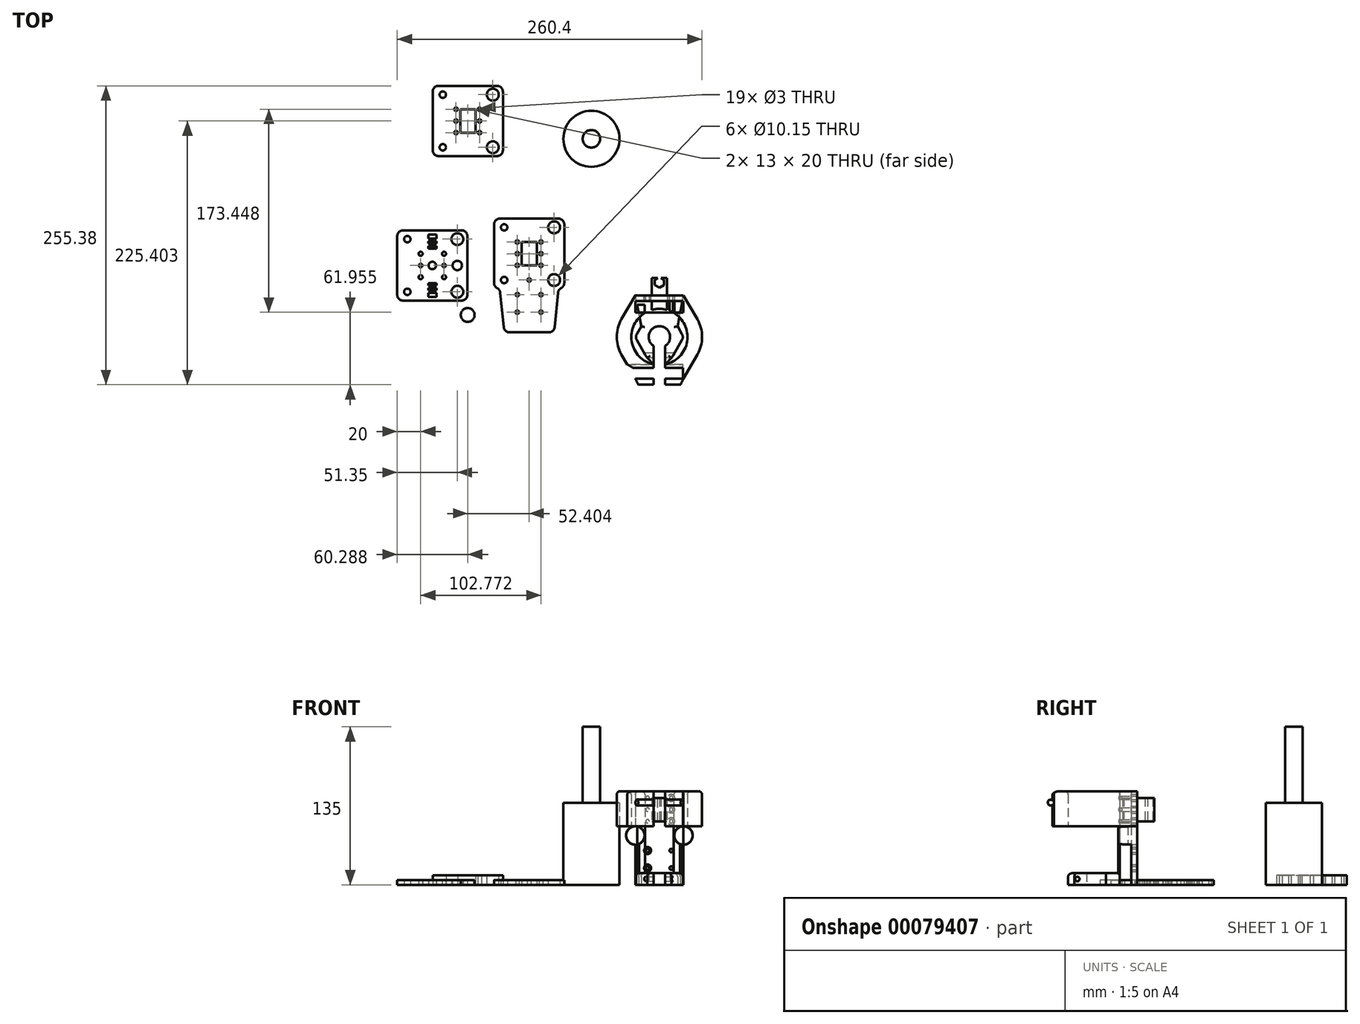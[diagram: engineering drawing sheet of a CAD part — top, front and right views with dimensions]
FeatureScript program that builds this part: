
annotation { "Feature Type Name" : "Feature", "Feature Type Description" : "" }
export const myFeature = defineFeature(function(context is Context, id is Id, definition is map)
    precondition{}
    {
        {
            var Q0;
            Q0=qCreatedBy(makeId("Top.planeOp"),FACE);
            var sketch = newSketch(context, id + "F0", { "sketchPlane" : qUnion([Q0])});
            skArc(sketch, "E0", {"start": v(24.79, -19.87) * mm, "mid": v(28.33, -18.4) * mm, "end": v(29.79, -14.87) * mm});
            skLineSegment(sketch, "E1", {"start": v(24.79, -19.87) * mm, "end": v(-25.21, -19.87) * mm});
            skArc(sketch, "E2", {"start": v(29.79, 35.13) * mm, "mid": v(28.33, 38.67) * mm, "end": v(24.79, 40.13) * mm});
            skLineSegment(sketch, "E3", {"start": v(29.79, 35.13) * mm, "end": v(29.79, -14.87) * mm});
            skArc(sketch, "E4", {"start": v(-25.21, 40.13) * mm, "mid": v(-28.75, 38.67) * mm, "end": v(-30.21, 35.13) * mm});
            skLineSegment(sketch, "E5", {"start": v(-25.21, 40.13) * mm, "end": v(24.79, 40.13) * mm});
            skArc(sketch, "E6", {"start": v(-30.21, -14.87) * mm, "mid": v(-28.75, -18.4) * mm, "end": v(-25.21, -19.87) * mm});
            skLineSegment(sketch, "E7", {"start": v(-30.21, -14.87) * mm, "end": v(-30.21, 35.13) * mm});
            skCircle(sketch, "E8", {"center": v(30, -32.16) * mm, "radius": 5.9 * mm});
            skCircle(sketch, "E9", {"center": v(-30, -32.16) * mm, "radius": 5.9 * mm});
            skLineSegment(sketch, "E10", {"start": v(-30.85, -40.13) * mm, "end": v(30.85, -40.13) * mm});
            skArc(sketch, "E11", {"start": v(30.85, -40.13) * mm, "mid": v(36.61, -37.74) * mm, "end": v(39, -31.98) * mm});
            skArc(sketch, "E12", {"start": v(39, -31.98) * mm, "mid": v(36.61, -26.22) * mm, "end": v(30.85, -23.83) * mm});
            skLineSegment(sketch, "E13", {"start": v(30.85, -23.83) * mm, "end": v(-30.85, -23.83) * mm});
            skArc(sketch, "E14", {"start": v(-30.85, -23.83) * mm, "mid": v(-36.61, -26.22) * mm, "end": v(-39, -31.98) * mm});
            skArc(sketch, "E15", {"start": v(-39, -31.98) * mm, "mid": v(-36.61, -37.74) * mm, "end": v(-30.85, -40.13) * mm});
            skCircle(sketch, "E16", {"center": v(21.14, 32.63) * mm, "radius": 5.08 * mm});
            skCircle(sketch, "E17", {"center": v(21.14, -12.37) * mm, "radius": 5.08 * mm});
            skCircle(sketch, "E18", {"center": v(-21.56, 32.63) * mm, "radius": 2.75 * mm});
            skCircle(sketch, "E19", {"center": v(-21.56, -12.37) * mm, "radius": 2.75 * mm});
            skCircle(sketch, "E20", {"center": v(-10.21, 20.13) * mm, "radius": 1.75 * mm});
            skCircle(sketch, "E21", {"center": v(-10.21, 0.13) * mm, "radius": 1.75 * mm});
            skCircle(sketch, "E22", {"center": v(9.79, 0.13) * mm, "radius": 1.75 * mm});
            skCircle(sketch, "E23", {"center": v(9.79, 20.13) * mm, "radius": 1.75 * mm});
            skLineSegment(sketch, "E24", {"start": v(-3.63, -6.88) * mm, "end": v(3.37, -6.88) * mm});
            skLineSegment(sketch, "E25", {"start": v(3.37, -6.88) * mm, "end": v(3.37, -4.88) * mm});
            skLineSegment(sketch, "E26", {"start": v(3.37, -4.88) * mm, "end": v(-3.63, -4.88) * mm});
            skLineSegment(sketch, "E27", {"start": v(-3.63, -4.88) * mm, "end": v(-3.63, -6.88) * mm});
            skLineSegment(sketch, "E28", {"start": v(-3.66, -11.08) * mm, "end": v(3.34, -11.08) * mm});
            skLineSegment(sketch, "E29", {"start": v(3.34, -11.08) * mm, "end": v(3.34, -9.08) * mm});
            skLineSegment(sketch, "E30", {"start": v(3.34, -9.08) * mm, "end": v(-3.66, -9.08) * mm});
            skLineSegment(sketch, "E31", {"start": v(-3.66, -9.08) * mm, "end": v(-3.66, -11.08) * mm});
            skLineSegment(sketch, "E32", {"start": v(3.35, -16.82) * mm, "end": v(3.35, -13.38) * mm});
            skLineSegment(sketch, "E33", {"start": v(3.35, -13.38) * mm, "end": v(-3.63, -13.38) * mm});
            skLineSegment(sketch, "E34", {"start": v(-3.63, 33.12) * mm, "end": v(3.37, 33.12) * mm});
            skLineSegment(sketch, "E35", {"start": v(3.37, 33.12) * mm, "end": v(3.37, 36.53) * mm});
            skLineSegment(sketch, "E36", {"start": v(3.37, 36.53) * mm, "end": v(-3.63, 36.52) * mm});
            skLineSegment(sketch, "E37", {"start": v(-3.63, 36.52) * mm, "end": v(-3.63, 33.12) * mm});
            skLineSegment(sketch, "E38", {"start": v(-3.66, 28.92) * mm, "end": v(3.34, 28.92) * mm});
            skLineSegment(sketch, "E39", {"start": v(3.34, 28.92) * mm, "end": v(3.34, 30.92) * mm});
            skLineSegment(sketch, "E40", {"start": v(3.34, 30.92) * mm, "end": v(-3.66, 30.92) * mm});
            skLineSegment(sketch, "E41", {"start": v(-3.66, 30.92) * mm, "end": v(-3.66, 28.92) * mm});
            skLineSegment(sketch, "E42", {"start": v(-3.63, 24.62) * mm, "end": v(3.37, 24.62) * mm});
            skLineSegment(sketch, "E43", {"start": v(3.37, 24.62) * mm, "end": v(3.37, 26.62) * mm});
            skLineSegment(sketch, "E44", {"start": v(3.37, 26.62) * mm, "end": v(-3.63, 26.62) * mm});
            skLineSegment(sketch, "E45", {"start": v(-3.63, 26.62) * mm, "end": v(-3.63, 24.62) * mm});
            skCircle(sketch, "E46", {"center": v(-10.21, 10.13) * mm, "radius": 1.5 * mm});
            skCircle(sketch, "E47", {"center": v(9.79, 10.13) * mm, "radius": 1.5 * mm});
            skCircle(sketch, "E48", {"center": v(-10.18, -31.98) * mm, "radius": 1.5 * mm});
            skCircle(sketch, "E49", {"center": v(9.82, -31.98) * mm, "radius": 1.5 * mm});
            skCircle(sketch, "E50", {"center": v(-0.21, 10.13) * mm, "radius": 3.2 * mm});
            skPoint(sketch, "E51", {"position": v(-3.63, 36.52) * mm});
            skLineSegment(sketch, "E52", {"start": v(-3.63, -16.82) * mm, "end": v(3.35, -16.82) * mm});
            skLineSegment(sketch, "E53", {"start": v(-3.63, -16.82) * mm, "end": v(-3.63, -13.38) * mm});
            skCircle(sketch, "E54", {"center": v(21.14, 10.13) * mm, "radius": 4 * mm});
            skLineSegment(sketch, "E55", {"start": v(112.48, 45.2) * mm, "end": v(112.48, -4.8) * mm});
            skLineSegment(sketch, "E56", {"start": v(57.48, 50.2) * mm, "end": v(107.48, 50.2) * mm});
            skLineSegment(sketch, "E57", {"start": v(52.48, -4.8) * mm, "end": v(52.48, 45.2) * mm});
            skCircle(sketch, "E58", {"center": v(103.83, 42.7) * mm, "radius": 5.08 * mm});
            skCircle(sketch, "E59", {"center": v(103.83, -2.3) * mm, "radius": 5.08 * mm});
            skCircle(sketch, "E60", {"center": v(61.13, -2.3) * mm, "radius": 2.75 * mm});
            skCircle(sketch, "E61", {"center": v(61.13, 42.7) * mm, "radius": 2.75 * mm});
            skArc(sketch, "E62", {"start": v(109.8, -9.23) * mm, "mid": v(111.76, -7.4) * mm, "end": v(112.48, -4.8) * mm});
            skArc(sketch, "E63", {"start": v(112.48, 45.2) * mm, "mid": v(111.02, 48.73) * mm, "end": v(107.48, 50.2) * mm});
            skArc(sketch, "E64", {"start": v(57.48, 50.2) * mm, "mid": v(53.95, 48.73) * mm, "end": v(52.48, 45.2) * mm});
            skArc(sketch, "E65", {"start": v(52.48, -4.8) * mm, "mid": v(53.95, -8.34) * mm, "end": v(57.48, -9.8) * mm});
            skLineSegment(sketch, "E66", {"start": v(82.48, -47) * mm, "end": v(82.48, -9.8) * mm, "construction": true});
            skLineSegment(sketch, "E67", {"start": v(82.48, -47) * mm, "end": v(99.3, -47) * mm});
            skLineSegment(sketch, "E68", {"start": v(107.15, -13.17) * mm, "end": v(104.27, -42.49) * mm});
            skPoint(sketch, "E69.visualSharp", {"position": v(107.48, -9.8) * mm});
            skArc(sketch, "E69.filletArc", {"start": v(109.8, -9.23) * mm, "mid": v(107.98, -10.87) * mm, "end": v(107.15, -13.17) * mm});
            skPoint(sketch, "E70.visualSharp", {"position": v(103.83, -47) * mm});
            skArc(sketch, "E70.filletArc", {"start": v(99.3, -47) * mm, "mid": v(102.66, -45.7) * mm, "end": v(104.27, -42.49) * mm});
            skLineSegment(sketch, "E71.MirrorCS", {"start": v(82.48, -47) * mm, "end": v(65.66, -47) * mm});
            skArc(sketch, "E72.MirrorCS", {"start": v(65.66, -47) * mm, "mid": v(62.3, -45.7) * mm, "end": v(60.69, -42.49) * mm});
            skLineSegment(sketch, "E73.MirrorCS", {"start": v(57.81, -13.17) * mm, "end": v(60.69, -42.49) * mm});
            skArc(sketch, "E74.MirrorCS", {"start": v(55.16, -9.23) * mm, "mid": v(56.98, -10.87) * mm, "end": v(57.81, -13.17) * mm});
            skLineSegment(sketch, "E75", {"start": v(82.48, 30.21) * mm, "end": v(87.48, 30.21) * mm});
            skLineSegment(sketch, "E76.bottom", {"start": v(87.48, 30.21) * mm, "end": v(77.48, 30.21) * mm});
            skLineSegment(sketch, "E77", {"start": v(92.56, 30.21) * mm, "end": v(92.56, 10.21) * mm, "construction": true});
            skLineSegment(sketch, "E78", {"start": v(87.48, 10.21) * mm, "end": v(77.48, 10.21) * mm});
            skCircle(sketch, "E79", {"center": v(92.56, 30.21) * mm, "radius": 1.5 * mm});
            skCircle(sketch, "E80", {"center": v(92.56, 20.21) * mm, "radius": 1.5 * mm});
            skCircle(sketch, "E81", {"center": v(92.56, 10.21) * mm, "radius": 1.5 * mm});
            skLineSegment(sketch, "E82", {"start": v(92.56, 10.21) * mm, "end": v(92.56, -14.79) * mm, "construction": true});
            skLineSegment(sketch, "E83", {"start": v(92.56, -14.79) * mm, "end": v(92.56, -29.79) * mm, "construction": true});
            skCircle(sketch, "E84", {"center": v(92.56, -14.79) * mm, "radius": 1.5 * mm});
            skCircle(sketch, "E85", {"center": v(92.56, -29.79) * mm, "radius": 1.5 * mm});
            skCircle(sketch, "E86.MirrorC", {"center": v(72.4, -14.79) * mm, "radius": 1.5 * mm});
            skCircle(sketch, "E87.MirrorC", {"center": v(72.4, -29.79) * mm, "radius": 1.5 * mm});
            skCircle(sketch, "E88.MirrorC", {"center": v(72.4, 10.21) * mm, "radius": 1.5 * mm});
            skCircle(sketch, "E89.MirrorC", {"center": v(72.4, 20.21) * mm, "radius": 1.5 * mm});
            skCircle(sketch, "E90.MirrorC", {"center": v(72.4, 30.21) * mm, "radius": 1.5 * mm});
            skLineSegment(sketch, "E91", {"start": v(60.08, 158.64) * mm, "end": v(60.08, 108.64) * mm});
            skLineSegment(sketch, "E92", {"start": v(5.08, 163.64) * mm, "end": v(55.08, 163.64) * mm});
            skLineSegment(sketch, "E93", {"start": v(0.08, 108.64) * mm, "end": v(0.08, 158.64) * mm});
            skCircle(sketch, "E94", {"center": v(51.43, 156.14) * mm, "radius": 5.08 * mm});
            skPoint(sketch, "E95.visualSharp", {"position": v(55.08, 103.64) * mm});
            skLineSegment(sketch, "E96", {"start": v(40.16, 143.66) * mm, "end": v(40.16, 123.66) * mm, "construction": true});
            skCircle(sketch, "E97", {"center": v(51.43, 111.14) * mm, "radius": 5.08 * mm});
            skCircle(sketch, "E98.MirrorC", {"center": v(20, 133.66) * mm, "radius": 1.5 * mm});
            skCircle(sketch, "E99", {"center": v(8.73, 111.14) * mm, "radius": 2.75 * mm});
            skCircle(sketch, "E100.MirrorC", {"center": v(20, 143.66) * mm, "radius": 1.5 * mm});
            skCircle(sketch, "E101", {"center": v(8.73, 156.14) * mm, "radius": 2.75 * mm});
            skCircle(sketch, "E102", {"center": v(40.16, 133.66) * mm, "radius": 1.5 * mm});
            skCircle(sketch, "E103.MirrorC", {"center": v(20, 123.66) * mm, "radius": 1.5 * mm});
            skLineSegment(sketch, "E104.bottom", {"start": v(35.08, 143.66) * mm, "end": v(25.08, 143.66) * mm});
            skArc(sketch, "E105", {"start": v(60.08, 158.64) * mm, "mid": v(58.61, 162.18) * mm, "end": v(55.08, 163.64) * mm});
            skLineSegment(sketch, "E106", {"start": v(35.08, 123.66) * mm, "end": v(25.08, 123.66) * mm});
            skArc(sketch, "E107", {"start": v(5.08, 163.64) * mm, "mid": v(1.54, 162.18) * mm, "end": v(0.08, 158.64) * mm});
            skCircle(sketch, "E108", {"center": v(40.16, 143.66) * mm, "radius": 1.5 * mm});
            skArc(sketch, "E109", {"start": v(0.08, 108.64) * mm, "mid": v(1.54, 105.1) * mm, "end": v(5.08, 103.64) * mm});
            skLineSegment(sketch, "E110", {"start": v(30.08, 143.66) * mm, "end": v(35.08, 143.66) * mm});
            skLineSegment(sketch, "E111", {"start": v(5.08, 103.64) * mm, "end": v(55.08, 103.64) * mm});
            skLineSegment(sketch, "E112", {"start": v(60.08, 108.64) * mm, "end": v(60.08, 108.64) * mm});
            skPoint(sketch, "E113.visualSharp", {"position": v(60.08, 103.64) * mm});
            skArc(sketch, "E113.filletArc", {"start": v(55.08, 103.64) * mm, "mid": v(58.61, 105.1) * mm, "end": v(60.08, 108.64) * mm});
            skCircle(sketch, "E114.MirrorC", {"center": v(40.16, 123.66) * mm, "radius": 1.5 * mm});
            skCircle(sketch, "E115", {"center": v(135.68, 118.4) * mm, "radius": 24 * mm});
            skCircle(sketch, "E116", {"center": v(135.68, 118.4) * mm, "radius": 7.5 * mm});
            skLineSegment(sketch, "E117", {"start": v(61.13, -2.3) * mm, "end": v(103.83, -2.3) * mm, "construction": true});
            skCircle(sketch, "E118", {"center": v(82.48, -2.3) * mm, "radius": 1.5 * mm});
            skArc(sketch, "E119.MirrorCS", {"start": v(112.48, -4.8) * mm, "mid": v(111.02, -8.34) * mm, "end": v(107.48, -9.8) * mm});
            skLineSegment(sketch, "E120", {"start": v(57.48, -9.8) * mm, "end": v(107.48, -9.8) * mm, "construction": true});
            skLineSegment(sketch, "E121.bottom", {"start": v(35.08, 123.66) * mm, "end": v(36.58, 123.66) * mm});
            skLineSegment(sketch, "E121.top", {"start": v(35.08, 143.66) * mm, "end": v(36.58, 143.66) * mm});
            skLineSegment(sketch, "E121.right", {"start": v(36.58, 123.66) * mm, "end": v(36.58, 143.66) * mm});
            skLineSegment(sketch, "E122", {"start": v(30.08, 123.66) * mm, "end": v(30.08, 133.29) * mm, "construction": true});
            skLineSegment(sketch, "E123.MirrorCS", {"start": v(23.58, 123.66) * mm, "end": v(23.58, 143.66) * mm});
            skLineSegment(sketch, "E124.MirrorCS", {"start": v(25.08, 123.66) * mm, "end": v(23.58, 123.66) * mm});
            skLineSegment(sketch, "E125.MirrorCS", {"start": v(25.08, 143.66) * mm, "end": v(23.58, 143.66) * mm});
            skLineSegment(sketch, "E126", {"start": v(87.48, 10.21) * mm, "end": v(88.98, 10.21) * mm});
            skLineSegment(sketch, "E127", {"start": v(88.98, 10.21) * mm, "end": v(88.98, 30.21) * mm});
            skLineSegment(sketch, "E128", {"start": v(88.98, 30.21) * mm, "end": v(87.48, 30.21) * mm});
            skLineSegment(sketch, "E129", {"start": v(82.48, 30.21) * mm, "end": v(82.48, 10.21) * mm, "construction": true});
            skLineSegment(sketch, "E130.MirrorCS", {"start": v(77.48, 10.21) * mm, "end": v(75.98, 10.21) * mm});
            skLineSegment(sketch, "E131.MirrorCS", {"start": v(75.98, 10.21) * mm, "end": v(75.98, 30.21) * mm});
            skLineSegment(sketch, "E132.MirrorCS", {"start": v(75.98, 30.21) * mm, "end": v(77.48, 30.21) * mm});
            skSolve(sketch);
        }
        {
            var Q0;
            Q0=makeQuery(id+"F0.imprint","IMPRINT",FACE,{"disambiguationData":[TD([[makeQuery(id+"F0.imprint","IMPRINT",EDGE,{"derivedFrom":sQuery(id+"F0.wireOp",EDGE,"E0")}),1.0]])]});
            var Q1;
            Q1=makeQuery(id+"F0.imprint","IMPRINT",FACE,{"disambiguationData":[TD([[makeQuery(id+"F0.imprint","IMPRINT",EDGE,{"derivedFrom":sQuery(id+"F0.wireOp",EDGE,"E8")}),1.0]])]});
            var Q2;
            Q2=makeQuery(id+"F0.imprint","IMPRINT",FACE,{"disambiguationData":[TD([[makeQuery(id+"F0.imprint","IMPRINT",EDGE,{"derivedFrom":sQuery(id+"F0.wireOp",EDGE,"f96d0108-ce3c-40f9-9041-a5f02a56c2c8")}),-1.0]])]});
            var Q3;
            Q3=makeQuery(id+"F0.imprint","IMPRINT",FACE,{"disambiguationData":[TD([[makeQuery(id+"F0.imprint","IMPRINT",EDGE,{"derivedFrom":sQuery(id+"F0.wireOp",EDGE,"fc6a74a1-8ae2-464b-8a54-e97a179053b1")}),1.0]])]});
            var Q4;
            Q4=makeQuery(id+"F0.imprint","IMPRINT",FACE,{"disambiguationData":[TD([[makeQuery(id+"F0.imprint","IMPRINT",EDGE,{"derivedFrom":sQuery(id+"F0.wireOp",EDGE,"E55")}),-1.0]])]});
            var Q5;
            Q5=makeQuery(id+"F0.imprint","IMPRINT",FACE,{"disambiguationData":[TD([[makeQuery(id+"F0.imprint","IMPRINT",EDGE,{"derivedFrom":sQuery(id+"F0.wireOp",EDGE,"E91")}),-1.0]])]});
            extrude(context, id + "F1", {"entities" : qUnion([Q0, Q1, Q2, Q3, Q4, Q5]), "depth" : 4 * mm});
        }
        {
            var Q0;
            Q0=qCreatedBy(makeId("Top.planeOp"),FACE);
            var sketch = newSketch(context, id + "F2", { "sketchPlane" : qUnion([Q0])});
            skCircle(sketch, "E133", {"center": v(193.74, -50.94) * mm, "radius": 9.15 * mm});
            skCircle(sketch, "E134.cCircle", {"center": v(193.74, -50.94) * mm, "radius": 17.99 * mm, "construction": true});
            skLineSegment(sketch, "E134.0", {"start": v(183.36, -32.95) * mm, "end": v(204.13, -32.95) * mm});
            skLineSegment(sketch, "E134.1", {"start": v(204.13, -32.95) * mm, "end": v(213.07, -48.44) * mm});
            skLineSegment(sketch, "E134.2", {"start": v(213.07, -53.44) * mm, "end": v(204.13, -68.93) * mm});
            skLineSegment(sketch, "E134.3", {"start": v(204.13, -68.93) * mm, "end": v(183.36, -68.93) * mm});
            skLineSegment(sketch, "E134.4", {"start": v(183.36, -68.93) * mm, "end": v(174.42, -53.44) * mm});
            skLineSegment(sketch, "E134.5", {"start": v(174.42, -48.44) * mm, "end": v(183.36, -32.95) * mm});
            skPoint(sketch, "E134.0.midPoint", {"position": v(193.74, -32.95) * mm});
            skCircle(sketch, "E135", {"center": v(193.74, -50.94) * mm, "radius": 24 * mm});
            skCircle(sketch, "E136.cCircle", {"center": v(193.74, -50.94) * mm, "radius": 35.58 * mm, "construction": true});
            skLineSegment(sketch, "E136.0", {"start": v(173.2, -15.36) * mm, "end": v(214.29, -15.36) * mm});
            skLineSegment(sketch, "E136.1", {"start": v(214.29, -15.36) * mm, "end": v(226.17, -35.94) * mm});
            skLineSegment(sketch, "E136.2", {"start": v(226.17, -65.94) * mm, "end": v(214.29, -86.52) * mm});
            skLineSegment(sketch, "E136.3", {"start": v(214.29, -86.52) * mm, "end": v(173.2, -86.52) * mm});
            skLineSegment(sketch, "E136.4", {"start": v(173.2, -86.52) * mm, "end": v(161.32, -65.94) * mm});
            skLineSegment(sketch, "E136.5", {"start": v(161.32, -35.94) * mm, "end": v(173.2, -15.36) * mm});
            skLineSegment(sketch, "E137", {"start": v(193.74, -50.94) * mm, "end": v(193.74, -100.84) * mm, "construction": true});
            skPoint(sketch, "E137.endSnap0", {"position": v(193.74, -86.52) * mm});
            skLineSegment(sketch, "E138", {"start": v(193.74, -100.84) * mm, "end": v(198.74, -100.84) * mm, "construction": true});
            skLineSegment(sketch, "E139", {"start": v(198.74, -100.84) * mm, "end": v(198.74, -58.6) * mm});
            skLineSegment(sketch, "E140", {"start": v(198.74, -100.84) * mm, "end": v(207.43, -100.84) * mm});
            skLineSegment(sketch, "E141", {"start": v(207.43, -100.84) * mm, "end": v(214.29, -86.52) * mm});
            skLineSegment(sketch, "E142.MirrorCS", {"start": v(188.74, -100.84) * mm, "end": v(188.74, -58.6) * mm});
            skLineSegment(sketch, "E143.MirrorCS", {"start": v(188.74, -100.84) * mm, "end": v(180.06, -100.84) * mm});
            skLineSegment(sketch, "E144.MirrorCS", {"start": v(180.06, -100.84) * mm, "end": v(173.2, -86.52) * mm});
            skLineSegment(sketch, "E145", {"start": v(183.36, -68.93) * mm, "end": v(188.74, -74.41) * mm});
            skLineSegment(sketch, "E146.MirrorCS", {"start": v(204.13, -68.93) * mm, "end": v(198.74, -74.41) * mm, "construction": true});
            skLineSegment(sketch, "E147.MirrorCS", {"start": v(204.13, -68.93) * mm, "end": v(198.74, -74.41) * mm});
            skLineSegment(sketch, "E148", {"start": v(193.74, -50.94) * mm, "end": v(203.74, -50.94) * mm, "construction": true});
            skLineSegment(sketch, "E149", {"start": v(203.74, -50.94) * mm, "end": v(203.74, -15.36) * mm, "construction": true});
            skLineSegment(sketch, "E150.MirrorCS", {"start": v(183.74, -50.94) * mm, "end": v(183.74, -15.36) * mm, "construction": true});
            skLineSegment(sketch, "E151", {"start": v(178.17, -41.94) * mm, "end": v(173.2, -15.36) * mm});
            skLineSegment(sketch, "E152", {"start": v(209.32, -41.94) * mm, "end": v(214.29, -15.36) * mm});
            skPoint(sketch, "E153.visualSharp", {"position": v(152.66, -50.94) * mm});
            skArc(sketch, "E153.filletArc", {"start": v(161.32, -35.94) * mm, "mid": v(157.3, -50.94) * mm, "end": v(161.32, -65.94) * mm});
            skPoint(sketch, "E154.visualSharp", {"position": v(234.83, -50.94) * mm});
            skArc(sketch, "E154.filletArc", {"start": v(226.17, -65.94) * mm, "mid": v(230.19, -50.94) * mm, "end": v(226.17, -35.94) * mm});
            skPoint(sketch, "E155.visualSharp", {"position": v(172.97, -50.94) * mm});
            skArc(sketch, "E155.filletArc", {"start": v(174.42, -48.44) * mm, "mid": v(173.75, -50.94) * mm, "end": v(174.42, -53.44) * mm});
            skPoint(sketch, "E156.visualSharp", {"position": v(214.51, -50.94) * mm});
            skArc(sketch, "E156.filletArc", {"start": v(213.07, -53.44) * mm, "mid": v(213.74, -50.94) * mm, "end": v(213.07, -48.44) * mm});
            skLineSegment(sketch, "E157", {"start": v(193.74, -15.36) * mm, "end": v(193.74, -7.36) * mm, "construction": true});
            skLineSegment(sketch, "E158", {"start": v(193.74, -7.36) * mm, "end": v(193.74, -4.36) * mm, "construction": true});
            skCircle(sketch, "E159.cCircle", {"center": v(193.74, -4.36) * mm, "radius": 4.5 * mm, "construction": true});
            skLineSegment(sketch, "E159.0", {"start": v(193.74, -8.86) * mm, "end": v(189.85, -6.6) * mm});
            skLineSegment(sketch, "E159.1", {"start": v(189.85, -6.6) * mm, "end": v(189.85, -2.1) * mm});
            skLineSegment(sketch, "E159.2", {"start": v(189.85, -2.1) * mm, "end": v(193.74, 0.14) * mm});
            skLineSegment(sketch, "E159.3", {"start": v(193.74, 0.14) * mm, "end": v(197.64, -2.1) * mm});
            skLineSegment(sketch, "E159.4", {"start": v(197.64, -2.1) * mm, "end": v(197.64, -6.6) * mm});
            skLineSegment(sketch, "E159.5", {"start": v(197.64, -6.6) * mm, "end": v(193.74, -8.86) * mm});
            skCircle(sketch, "E160", {"center": v(193.74, -4.36) * mm, "radius": 2.5 * mm, "construction": true});
            skSolve(sketch);
        }
        {
            var Q0;
            {var subQ0=sQuery(id+"F2.wireOp",EDGE,"96ee02a5-edc4-4475-906e-b3a8b5a1a6cf");var subQ1=sQuery(id+"F2.wireOp",EDGE,"E135");var subQ2=makeQuery(id+"F2.imprint","INTERSECT",VERTEX,{"derivedFrom":[subQ1,subQ0]});Q0=makeQuery(id+"F2.imprint","IMPRINT",FACE,{"disambiguationData":[TD([[makeQuery(id+"F2.imprint","IMPRINT",EDGE,{"disambiguationData":[TD([[subQ2,1.0]])],"derivedFrom":subQ1}),-1.0]])]});}
            var Q1;
            {var subQ5=sQuery(id+"F2.wireOp",EDGE,"E136.0");Q1=makeQuery(id+"F2.imprint","IMPRINT",FACE,{"disambiguationData":[TD([[makeQuery(id+"F2.imprint","IMPRINT",EDGE,{"derivedFrom":subQ5}),-1.0]])]});}
            var Q2;
            {var subQ11=sQuery(id+"F2.wireOp",EDGE,"E134.0");Q2=makeQuery(id+"F2.imprint","IMPRINT",FACE,{"disambiguationData":[TD([[makeQuery(id+"F2.imprint","IMPRINT",EDGE,{"derivedFrom":subQ11}),-1.0]])]});}
            var Q3;
            {var subQ8=sQuery(id+"F2.wireOp",EDGE,"E134.0");Q3=makeQuery(id+"F2.imprint","IMPRINT",FACE,{"disambiguationData":[TD([[makeQuery(id+"F2.imprint","IMPRINT",EDGE,{"derivedFrom":subQ8}),1.0]])]});}
            var Q4;
            {var subQ0=sQuery(id+"F2.wireOp",EDGE,"E147.MirrorCS");Q4=makeQuery(id+"F2.imprint","IMPRINT",FACE,{"disambiguationData":[TD([[makeQuery(id+"F2.imprint","IMPRINT",EDGE,{"derivedFrom":subQ0}),-1.0]])]});}
            var Q5;
            {var subQ0=sQuery(id+"F2.wireOp",EDGE,"E145");Q5=makeQuery(id+"F2.imprint","IMPRINT",FACE,{"disambiguationData":[TD([[makeQuery(id+"F2.imprint","IMPRINT",EDGE,{"derivedFrom":subQ0}),1.0]])]});}
            extrude(context, id + "F3", {"entities" : qUnion([Q0, Q1, Q2, Q3, Q4, Q5]), "depth" : 10 * mm});
        }
        {
            var Q0;
            {var subQ5=sQuery(id+"F2.wireOp",EDGE,"E136.0");Q0=makeQuery(id+"F2.imprint","IMPRINT",FACE,{"disambiguationData":[TD([[makeQuery(id+"F2.imprint","IMPRINT",EDGE,{"derivedFrom":subQ5}),-1.0]])]});}
            extrude(context, id + "F4", {"entities" : qUnion([Q0]), "operationType" : NewBodyOperationType.ADD, "depth" : 80 * mm, "hasSecondDirection" : true, "secondDirectionOppositeDirection" : false, "secondDirectionDepth" : 10 * mm});
        }
        {
            var Q0;
            {var subQ1=sQuery(id+"F2.wireOp",EDGE,"E136.4");Q0=makeQuery(id+"F2.imprint","IMPRINT",FACE,{"disambiguationData":[TD([[makeQuery(id+"F2.imprint","IMPRINT",EDGE,{"derivedFrom":subQ1}),-1.0]])]});}
            var Q1;
            {var subQ4=sQuery(id+"F2.wireOp",EDGE,"E143.MirrorCS");Q1=makeQuery(id+"F2.imprint","IMPRINT",FACE,{"disambiguationData":[TD([[makeQuery(id+"F2.imprint","IMPRINT",EDGE,{"derivedFrom":subQ4}),-1.0]])]});}
            var Q2;
            {var subQ4=sQuery(id+"F2.wireOp",EDGE,"E140");Q2=makeQuery(id+"F2.imprint","IMPRINT",FACE,{"disambiguationData":[TD([[makeQuery(id+"F2.imprint","IMPRINT",EDGE,{"derivedFrom":subQ4}),1.0]])]});}
            var Q3;
            {var subQ6=sQuery(id+"F2.wireOp",EDGE,"E136.1");Q3=makeQuery(id+"F2.imprint","IMPRINT",FACE,{"disambiguationData":[TD([[makeQuery(id+"F2.imprint","IMPRINT",EDGE,{"derivedFrom":subQ6}),-1.0]])]});}
            var Q4;
            {var subQ5=sQuery(id+"F2.wireOp",EDGE,"E136.0");Q4=makeQuery(id+"F2.imprint","IMPRINT",FACE,{"disambiguationData":[TD([[makeQuery(id+"F2.imprint","IMPRINT",EDGE,{"derivedFrom":subQ5}),-1.0]])]});}
            extrude(context, id + "F5", {"entities" : qUnion([Q0, Q1, Q2, Q3, Q4]), "operationType" : NewBodyOperationType.ADD, "depth" : 80 * mm, "hasSecondDirection" : true, "secondDirectionOppositeDirection" : false, "secondDirectionDepth" : 50 * mm});
        }
        {
            var Q0;
            {var subQ0=sQuery(id+"F2.wireOp",EDGE,"E136.0");Q0=makeQuery(id+"F4.boolean.opBoolean","MERGE",FACE,{"derivedFrom":[makeQuery(id+"F3.opExtrude","SWEPT_FACE",FACE,{"disambiguationData":[OSD([subQ0])]}),makeQuery(id+"F4.opExtrude","SWEPT_FACE",FACE,{"disambiguationData":[OSD([subQ0])]})]});}
            var sketch = newSketch(context, id + "F6", { "sketchPlane" : qUnion([Q0])});
            skLineSegment(sketch, "E161", {"start": v(-193.74, 64.3) * mm, "end": v(-198.74, 64.3) * mm, "construction": true});
            skLineSegment(sketch, "E162", {"start": v(-198.74, 64.3) * mm, "end": v(-198.74, 54.3) * mm, "construction": true});
            skLineSegment(sketch, "E163", {"start": v(-198.74, 54.3) * mm, "end": v(-193.74, 54.3) * mm, "construction": true});
            skLineSegment(sketch, "E164.bottom", {"start": v(-198.74, 54.3) * mm, "end": v(-188.74, 54.3) * mm});
            skLineSegment(sketch, "E164.top", {"start": v(-198.74, 74.3) * mm, "end": v(-188.74, 74.3) * mm});
            skLineSegment(sketch, "E165", {"start": v(-188.74, 74.3) * mm, "end": v(-183.66, 74.3) * mm, "construction": true});
            skCircle(sketch, "E166", {"center": v(-183.66, 74.3) * mm, "radius": 1.5 * mm});
            skCircle(sketch, "E167", {"center": v(-183.66, 64.3) * mm, "radius": 1.5 * mm});
            skCircle(sketch, "E168", {"center": v(-183.66, 54.3) * mm, "radius": 1.5 * mm});
            skCircle(sketch, "E169", {"center": v(-173.2, 42.14) * mm, "radius": 7.86 * mm});
            skLineSegment(sketch, "E170", {"start": v(-193.74, 0) * mm, "end": v(-193.74, 29.82) * mm, "construction": true});
            skCircle(sketch, "E171.MirrorC", {"center": v(-214.29, 42.14) * mm, "radius": 7.86 * mm});
            skLineSegment(sketch, "E172", {"start": v(-193.74, 29.82) * mm, "end": v(-193.74, 54.3) * mm, "construction": true});
            skLineSegment(sketch, "E173", {"start": v(-203.82, 54.3) * mm, "end": v(-203.82, 29.3) * mm, "construction": true});
            skLineSegment(sketch, "E174", {"start": v(-203.82, 29.3) * mm, "end": v(-203.82, 14.3) * mm, "construction": true});
            skCircle(sketch, "E175", {"center": v(-203.82, 29.3) * mm, "radius": 1.5 * mm});
            skCircle(sketch, "E176", {"center": v(-203.82, 14.3) * mm, "radius": 1.5 * mm});
            skCircle(sketch, "E177.MirrorC", {"center": v(-183.66, 29.3) * mm, "radius": 1.5 * mm});
            skCircle(sketch, "E178.MirrorC", {"center": v(-183.66, 14.3) * mm, "radius": 1.5 * mm});
            skCircle(sketch, "E179", {"center": v(-183.66, 74.3) * mm, "radius": 3 * mm});
            skCircle(sketch, "E180", {"center": v(-183.66, 64.3) * mm, "radius": 3 * mm});
            skCircle(sketch, "E181", {"center": v(-183.66, 54.3) * mm, "radius": 3 * mm});
            skCircle(sketch, "E182", {"center": v(-183.66, 29.3) * mm, "radius": 3 * mm});
            skCircle(sketch, "E183", {"center": v(-183.66, 14.3) * mm, "radius": 3 * mm});
            skCircle(sketch, "E184.MirrorC", {"center": v(-203.82, 29.3) * mm, "radius": 3 * mm});
            skCircle(sketch, "E185.MirrorC", {"center": v(-203.82, 14.3) * mm, "radius": 3 * mm});
            skCircle(sketch, "E186.MirrorC", {"center": v(-203.82, 54.3) * mm, "radius": 3 * mm});
            skCircle(sketch, "E187.MirrorC", {"center": v(-203.82, 64.3) * mm, "radius": 3 * mm});
            skCircle(sketch, "E188.MirrorC", {"center": v(-203.82, 74.3) * mm, "radius": 3 * mm});
            skCircle(sketch, "E189.MirrorC", {"center": v(-203.82, 54.3) * mm, "radius": 1.5 * mm});
            skCircle(sketch, "E190.MirrorC", {"center": v(-203.82, 64.3) * mm, "radius": 1.5 * mm});
            skCircle(sketch, "E191.MirrorC", {"center": v(-203.82, 74.3) * mm, "radius": 1.5 * mm});
            skLineSegment(sketch, "E192", {"start": v(-193.74, 74.3) * mm, "end": v(-193.74, 54.3) * mm, "construction": true});
            skLineSegment(sketch, "E193.bottom", {"start": v(-198.74, 74.3) * mm, "end": v(-200.24, 74.3) * mm, "construction": true});
            skLineSegment(sketch, "E193.top", {"start": v(-198.74, 54.3) * mm, "end": v(-200.24, 54.3) * mm, "construction": true});
            skLineSegment(sketch, "E193.right", {"start": v(-200.24, 74.3) * mm, "end": v(-200.24, 54.3) * mm, "construction": true});
            skLineSegment(sketch, "E194.bottom", {"start": v(-198.74, 74.3) * mm, "end": v(-200.24, 74.3) * mm});
            skLineSegment(sketch, "E194.top", {"start": v(-198.74, 54.3) * mm, "end": v(-200.24, 54.3) * mm});
            skLineSegment(sketch, "E194.right", {"start": v(-200.24, 74.3) * mm, "end": v(-200.24, 54.3) * mm});
            skLineSegment(sketch, "E195.MirrorCS", {"start": v(-188.74, 74.3) * mm, "end": v(-187.24, 74.3) * mm});
            skLineSegment(sketch, "E196.MirrorCS", {"start": v(-187.24, 74.3) * mm, "end": v(-187.24, 54.3) * mm});
            skLineSegment(sketch, "E197.MirrorCS", {"start": v(-188.74, 54.3) * mm, "end": v(-187.24, 54.3) * mm});
            skSolve(sketch);
        }
        {
            var Q0;
            Q0=makeQuery(id+"F6.imprint","IMPRINT",FACE,{"disambiguationData":[TD([[makeQuery(id+"F6.imprint","IMPRINT",EDGE,{"derivedFrom":sQuery(id+"F6.wireOp",EDGE,"E168")}),1.0]])]});
            var Q1;
            Q1=makeQuery(id+"F6.imprint","IMPRINT",FACE,{"disambiguationData":[TD([[makeQuery(id+"F6.imprint","IMPRINT",EDGE,{"derivedFrom":sQuery(id+"F6.wireOp",EDGE,"E167")}),1.0]])]});
            var Q2;
            Q2=makeQuery(id+"F6.imprint","IMPRINT",FACE,{"disambiguationData":[TD([[makeQuery(id+"F6.imprint","IMPRINT",EDGE,{"derivedFrom":sQuery(id+"F6.wireOp",EDGE,"E166")}),1.0]])]});
            var Q3;
            Q3=makeQuery(id+"F6.imprint","IMPRINT",FACE,{"disambiguationData":[TD([[makeQuery(id+"F6.imprint","IMPRINT",EDGE,{"derivedFrom":sQuery(id+"F6.wireOp",EDGE,"45766864-c449-461b-9b77-59a764d4195f0.MirrorC")}),-1.0]])]});
            var Q4;
            Q4=makeQuery(id+"F6.imprint","IMPRINT",FACE,{"disambiguationData":[TD([[makeQuery(id+"F6.imprint","IMPRINT",EDGE,{"derivedFrom":sQuery(id+"F6.wireOp",EDGE,"dd78de97-23d6-4229-883f-769f5d6694050.MirrorC")}),-1.0]])]});
            var Q5;
            Q5=makeQuery(id+"F6.imprint","IMPRINT",FACE,{"disambiguationData":[TD([[makeQuery(id+"F6.imprint","IMPRINT",EDGE,{"derivedFrom":sQuery(id+"F6.wireOp",EDGE,"2f0e754c-4723-4be7-9447-68277993e2870.MirrorC")}),-1.0]])]});
            var Q6;
            Q6=makeQuery(id+"F6.imprint","IMPRINT",FACE,{"disambiguationData":[TD([[makeQuery(id+"F6.imprint","IMPRINT",EDGE,{"derivedFrom":sQuery(id+"F6.wireOp",EDGE,"E189.MirrorC")}),-1.0]])]});
            var Q7;
            Q7=makeQuery(id+"F6.imprint","IMPRINT",FACE,{"disambiguationData":[TD([[makeQuery(id+"F6.imprint","IMPRINT",EDGE,{"derivedFrom":sQuery(id+"F6.wireOp",EDGE,"E190.MirrorC")}),-1.0]])]});
            var Q8;
            Q8=makeQuery(id+"F6.imprint","IMPRINT",FACE,{"disambiguationData":[TD([[makeQuery(id+"F6.imprint","IMPRINT",EDGE,{"derivedFrom":sQuery(id+"F6.wireOp",EDGE,"E191.MirrorC")}),-1.0]])]});
            var Q9;
            Q9=makeQuery(id+"F6.imprint","IMPRINT",FACE,{"disambiguationData":[TD([[makeQuery(id+"F6.imprint","IMPRINT",EDGE,{"derivedFrom":sQuery(id+"F6.wireOp",EDGE,"E175")}),1.0]])]});
            var Q10;
            Q10=makeQuery(id+"F6.imprint","IMPRINT",FACE,{"disambiguationData":[TD([[makeQuery(id+"F6.imprint","IMPRINT",EDGE,{"derivedFrom":sQuery(id+"F6.wireOp",EDGE,"E177.MirrorC")}),-1.0]])]});
            var Q11;
            Q11=makeQuery(id+"F6.imprint","IMPRINT",FACE,{"disambiguationData":[TD([[makeQuery(id+"F6.imprint","IMPRINT",EDGE,{"derivedFrom":sQuery(id+"F6.wireOp",EDGE,"E178.MirrorC")}),-1.0]])]});
            var Q12;
            Q12=makeQuery(id+"F6.imprint","IMPRINT",FACE,{"disambiguationData":[TD([[makeQuery(id+"F6.imprint","IMPRINT",EDGE,{"derivedFrom":sQuery(id+"F6.wireOp",EDGE,"E176")}),1.0]])]});
            extrude(context, id + "F7", {"entities" : qUnion([Q0, Q1, Q2, Q3, Q4, Q5, Q6, Q7, Q8, Q9, Q10, Q11, Q12]), "operationType" : NewBodyOperationType.REMOVE, "oppositeDirection" : true, "depth" : 25 * mm});
        }
        {
            var Q0;
            Q0=makeQuery(id+"F6.imprint","IMPRINT",FACE,{"disambiguationData":[TD([[makeQuery(id+"F6.imprint","IMPRINT",EDGE,{"derivedFrom":sQuery(id+"F6.wireOp",EDGE,"E164.bottom")}),1.0]])]});
            extrude(context, id + "F8", {"entities" : qUnion([Q0]), "operationType" : NewBodyOperationType.ADD, "depth" : 14.72 * mm});
        }
        {
            var Q0;
            {var subQ0=sQuery(id+"F6.wireOp",EDGE,"E171.MirrorC");var subQ1=sQuery(id+"F2.wireOp",EDGE,"E136.0");var subQ2=sQuery(id+"F2.wireOp",EDGE,"E152");var subQ3=sQuery(id+"F2.wireOp",EDGE,"E142.MirrorCS");var subQ4=sQuery(id+"F2.wireOp",EDGE,"E139");var subQ5=sQuery(id+"F2.wireOp",EDGE,"E136.1");var subQ6=makeQuery(id+"F4.boolean.opBoolean","MERGE",EDGE,{"derivedFrom":[makeQuery(id+"F3.opExtrude","SWEPT_EDGE",EDGE,{"disambiguationData":[OSD([subQ1,subQ5,subQ2])]}),makeQuery(id+"F4.opExtrude","SWEPT_EDGE",EDGE,{"disambiguationData":[OSD([subQ1,subQ5,subQ2])]})]});var subQ7=makeQuery(id+"F5.boolean.opBoolean","SPLIT",EDGE,{"disambiguationData":[TD([makeQuery(id+"F3.opExtrude","CAP_FACE",FACE,{"disambiguationData":[OSD([sQuery(id+"F2.wireOp",EDGE,"E133"),sQuery(id+"F2.wireOp",EDGE,"E134.1"),sQuery(id+"F2.wireOp",EDGE,"E134.2"),sQuery(id+"F2.wireOp",EDGE,"E134.4"),sQuery(id+"F2.wireOp",EDGE,"E134.5"),subQ1,subQ4,subQ3,sQuery(id+"F2.wireOp",EDGE,"E145"),sQuery(id+"F2.wireOp",EDGE,"E147.MirrorCS"),sQuery(id+"F2.wireOp",EDGE,"E151"),subQ2])],"isStart":true})])],"derivedFrom":subQ6});var subQ9=makeQuery(id+"F6.imprint","INTERSECT",VERTEX,{"derivedFrom":[subQ7,subQ0]});Q0=makeQuery(id+"F6.imprint","IMPRINT",FACE,{"disambiguationData":[TD([[makeQuery(id+"F6.imprint","IMPRINT",EDGE,{"disambiguationData":[TD([[subQ9,1.0]])],"derivedFrom":subQ0}),-1.0]])]});}
            var Q1;
            {var subQ0=sQuery(id+"F6.wireOp",EDGE,"E169");var subQ1=sQuery(id+"F2.wireOp",EDGE,"E136.0");var subQ2=sQuery(id+"F2.wireOp",EDGE,"E151");var subQ3=sQuery(id+"F2.wireOp",EDGE,"E142.MirrorCS");var subQ4=sQuery(id+"F2.wireOp",EDGE,"E139");var subQ5=sQuery(id+"F2.wireOp",EDGE,"E136.5");var subQ6=makeQuery(id+"F4.boolean.opBoolean","MERGE",EDGE,{"derivedFrom":[makeQuery(id+"F3.opExtrude","SWEPT_EDGE",EDGE,{"disambiguationData":[OSD([subQ1,subQ5,subQ2])]}),makeQuery(id+"F4.opExtrude","SWEPT_EDGE",EDGE,{"disambiguationData":[OSD([subQ1,subQ5,subQ2])]})]});var subQ7=makeQuery(id+"F5.boolean.opBoolean","SPLIT",EDGE,{"disambiguationData":[TD([makeQuery(id+"F3.opExtrude","CAP_FACE",FACE,{"disambiguationData":[OSD([sQuery(id+"F2.wireOp",EDGE,"E133"),sQuery(id+"F2.wireOp",EDGE,"E134.1"),sQuery(id+"F2.wireOp",EDGE,"E134.2"),sQuery(id+"F2.wireOp",EDGE,"E134.4"),sQuery(id+"F2.wireOp",EDGE,"E134.5"),subQ1,subQ4,subQ3,sQuery(id+"F2.wireOp",EDGE,"E145"),sQuery(id+"F2.wireOp",EDGE,"E147.MirrorCS"),subQ2,sQuery(id+"F2.wireOp",EDGE,"E152")])],"isStart":true})])],"derivedFrom":subQ6});var subQ9=makeQuery(id+"F6.imprint","INTERSECT",VERTEX,{"derivedFrom":[subQ7,subQ0]});Q1=makeQuery(id+"F6.imprint","IMPRINT",FACE,{"disambiguationData":[TD([[makeQuery(id+"F6.imprint","IMPRINT",EDGE,{"disambiguationData":[TD([[subQ9,1.0]])],"derivedFrom":subQ0}),1.0]])]});}
            extrude(context, id + "F9", {"entities" : qUnion([Q0, Q1]), "operationType" : NewBodyOperationType.REMOVE, "oppositeDirection" : true, "depth" : 8 * mm});
        }
        {
            var Q0;
            Q0=makeQuery(id+"F2.imprint","IMPRINT",FACE,{"disambiguationData":[TD([[makeQuery(id+"F2.imprint","IMPRINT",EDGE,{"derivedFrom":sQuery(id+"F2.wireOp",EDGE,"E159.0")}),-1.0]])]});
            extrude(context, id + "F10", {"entities" : qUnion([Q0]), "operationType" : NewBodyOperationType.REMOVE, "depth" : 80 * mm});
        }
        {
            var Q0;
            Q0=makeQuery(id+"F5.opExtrude","CAP_EDGE",EDGE,{"disambiguationData":[OSD([sQuery(id+"F2.wireOp",EDGE,"E140")])],"isStart":false});
            var Q1;
            Q1=makeQuery(id+"F5.opExtrude","CAP_EDGE",EDGE,{"disambiguationData":[OSD([sQuery(id+"F2.wireOp",EDGE,"E141")])],"isStart":false});
            var Q2;
            Q2=makeQuery(id+"F5.opExtrude","CAP_EDGE",EDGE,{"disambiguationData":[OSD([sQuery(id+"F2.wireOp",EDGE,"E136.1")])],"isStart":false});
            var Q3;
            Q3=makeQuery(id+"F5.opExtrude","CAP_EDGE",EDGE,{"disambiguationData":[OSD([sQuery(id+"F2.wireOp",EDGE,"E136.5")])],"isStart":false});
            var Q4;
            Q4=makeQuery(id+"F5.opExtrude","CAP_EDGE",EDGE,{"disambiguationData":[OSD([sQuery(id+"F2.wireOp",EDGE,"E153.filletArc")])],"isStart":false});
            var Q5;
            Q5=makeQuery(id+"F4.opExtrude","CAP_EDGE",EDGE,{"disambiguationData":[OSD([sQuery(id+"F2.wireOp",EDGE,"E135")])],"isStart":false});
            var Q6;
            Q6=makeQuery(id+"F4.opExtrude","CAP_EDGE",EDGE,{"disambiguationData":[OSD([sQuery(id+"F2.wireOp",EDGE,"E151")])],"isStart":false});
            var Q7;
            Q7=makeQuery(id+"F4.opExtrude","CAP_EDGE",EDGE,{"disambiguationData":[OSD([sQuery(id+"F2.wireOp",EDGE,"E152")])],"isStart":false});
            var Q8;
            Q8=makeQuery(id+"F3.opExtrude","CAP_EDGE",EDGE,{"disambiguationData":[OSD([sQuery(id+"F2.wireOp",EDGE,"E152")])],"isStart":false});
            var Q9;
            Q9=makeQuery(id+"F3.opExtrude","CAP_EDGE",EDGE,{"disambiguationData":[OSD([sQuery(id+"F2.wireOp",EDGE,"E151")])],"isStart":false});
            var Q10;
            {var subQ0=sQuery(id+"F2.wireOp",EDGE,"E152");var subQ1=sQuery(id+"F2.wireOp",EDGE,"E135");var subQ2=sQuery(id+"F2.wireOp",EDGE,"E142.MirrorCS");var subQ3=sQuery(id+"F2.wireOp",EDGE,"E139");var subQ4=sQuery(id+"F2.wireOp",EDGE,"E136.0");Q10=makeQuery(id+"F5.boolean.opBoolean","SPLIT",EDGE,{"disambiguationData":[TD([makeQuery(id+"F3.opExtrude","CAP_FACE",FACE,{"disambiguationData":[OSD([sQuery(id+"F2.wireOp",EDGE,"E133"),sQuery(id+"F2.wireOp",EDGE,"E134.1"),sQuery(id+"F2.wireOp",EDGE,"E134.2"),sQuery(id+"F2.wireOp",EDGE,"E134.4"),sQuery(id+"F2.wireOp",EDGE,"E134.5"),subQ4,subQ3,subQ2,sQuery(id+"F2.wireOp",EDGE,"E145"),sQuery(id+"F2.wireOp",EDGE,"E147.MirrorCS"),sQuery(id+"F2.wireOp",EDGE,"E151"),subQ0,sQuery(id+"F2.wireOp",EDGE,"E155.filletArc"),sQuery(id+"F2.wireOp",EDGE,"E156.filletArc")])],"isStart":false})])],"derivedFrom":makeQuery(id+"F4.opExtrude","SWEPT_EDGE",EDGE,{"disambiguationData":[OSD([subQ1,subQ0])]})});}
            var Q11;
            {var subQ0=sQuery(id+"F2.wireOp",EDGE,"E152");var subQ1=sQuery(id+"F2.wireOp",EDGE,"E136.0");var subQ2=sQuery(id+"F2.wireOp",EDGE,"E135");Q11=makeQuery(id+"F5.boolean.opBoolean","SPLIT",EDGE,{"disambiguationData":[TD([makeQuery(id+"F4.opExtrude","CAP_FACE",FACE,{"disambiguationData":[OSD([subQ2,subQ1,sQuery(id+"F2.wireOp",EDGE,"E151"),subQ0])],"isStart":false})])],"derivedFrom":makeQuery(id+"F4.opExtrude","SWEPT_EDGE",EDGE,{"disambiguationData":[OSD([subQ2,subQ0])]})});}
            var Q12;
            Q12=makeQuery(id+"F3.opExtrude","CAP_EDGE",EDGE,{"disambiguationData":[OSD([sQuery(id+"F2.wireOp",EDGE,"E134.1")])],"isStart":false});
            var Q13;
            Q13=makeQuery(id+"F3.opExtrude","CAP_EDGE",EDGE,{"disambiguationData":[OSD([sQuery(id+"F2.wireOp",EDGE,"E134.2")])],"isStart":false});
            var Q14;
            Q14=makeQuery(id+"F3.opExtrude","CAP_EDGE",EDGE,{"disambiguationData":[OSD([sQuery(id+"F2.wireOp",EDGE,"E147.MirrorCS")])],"isStart":false});
            var Q15;
            Q15=makeQuery(id+"F3.opExtrude","CAP_EDGE",EDGE,{"disambiguationData":[OSD([sQuery(id+"F2.wireOp",EDGE,"E156.filletArc")])],"isStart":false});
            var Q16;
            Q16=makeQuery(id+"F3.opExtrude","CAP_EDGE",EDGE,{"disambiguationData":[OSD([sQuery(id+"F2.wireOp",EDGE,"E134.5")])],"isStart":false});
            var Q17;
            Q17=makeQuery(id+"F3.opExtrude","CAP_EDGE",EDGE,{"disambiguationData":[OSD([sQuery(id+"F2.wireOp",EDGE,"E155.filletArc")])],"isStart":false});
            var Q18;
            Q18=makeQuery(id+"F3.opExtrude","CAP_EDGE",EDGE,{"disambiguationData":[OSD([sQuery(id+"F2.wireOp",EDGE,"E134.4")])],"isStart":false});
            var Q19;
            Q19=makeQuery(id+"F3.opExtrude","CAP_EDGE",EDGE,{"disambiguationData":[OSD([sQuery(id+"F2.wireOp",EDGE,"E145")])],"isStart":false});
            var Q20;
            {var subQ0=sQuery(id+"F2.wireOp",EDGE,"E151");var subQ1=sQuery(id+"F2.wireOp",EDGE,"E136.0");var subQ2=sQuery(id+"F2.wireOp",EDGE,"E135");Q20=makeQuery(id+"F5.boolean.opBoolean","SPLIT",EDGE,{"disambiguationData":[TD([makeQuery(id+"F4.opExtrude","CAP_FACE",FACE,{"disambiguationData":[OSD([subQ2,subQ1,subQ0,sQuery(id+"F2.wireOp",EDGE,"E152")])],"isStart":false})])],"derivedFrom":makeQuery(id+"F4.opExtrude","SWEPT_EDGE",EDGE,{"disambiguationData":[OSD([subQ2,subQ0])]})});}
            var Q21;
            {var subQ0=sQuery(id+"F2.wireOp",EDGE,"E151");var subQ1=sQuery(id+"F2.wireOp",EDGE,"E135");var subQ2=sQuery(id+"F2.wireOp",EDGE,"E142.MirrorCS");var subQ3=sQuery(id+"F2.wireOp",EDGE,"E139");var subQ4=sQuery(id+"F2.wireOp",EDGE,"E136.0");Q21=makeQuery(id+"F5.boolean.opBoolean","SPLIT",EDGE,{"disambiguationData":[TD([makeQuery(id+"F3.opExtrude","CAP_FACE",FACE,{"disambiguationData":[OSD([sQuery(id+"F2.wireOp",EDGE,"E133"),sQuery(id+"F2.wireOp",EDGE,"E134.1"),sQuery(id+"F2.wireOp",EDGE,"E134.2"),sQuery(id+"F2.wireOp",EDGE,"E134.4"),sQuery(id+"F2.wireOp",EDGE,"E134.5"),subQ4,subQ3,subQ2,sQuery(id+"F2.wireOp",EDGE,"E145"),sQuery(id+"F2.wireOp",EDGE,"E147.MirrorCS"),subQ0,sQuery(id+"F2.wireOp",EDGE,"E152"),sQuery(id+"F2.wireOp",EDGE,"E155.filletArc"),sQuery(id+"F2.wireOp",EDGE,"E156.filletArc")])],"isStart":false})])],"derivedFrom":makeQuery(id+"F4.opExtrude","SWEPT_EDGE",EDGE,{"disambiguationData":[OSD([subQ1,subQ0])]})});}
            var Q22;
            Q22=makeQuery(id+"F5.opExtrude","CAP_EDGE",EDGE,{"disambiguationData":[OSD([sQuery(id+"F2.wireOp",EDGE,"E143.MirrorCS")])],"isStart":false});
            fillet(context, id + "F11", {"entities" : qUnion([Q0, Q1, Q2, Q3, Q4, Q5, Q6, Q7, Q8, Q9, Q10, Q11, Q12, Q13, Q14, Q15, Q16, Q17, Q18, Q19, Q20, Q21, Q22]), "radius" : 3 * mm, "tangentPropagation" : true, "allowEdgeOverflow" : false});
        }
        {
            var Q0;
            Q0=makeQuery(id+"F3.opExtrude","SWEPT_FACE",FACE,{"disambiguationData":[OSD([sQuery(id+"F2.wireOp",EDGE,"E142.MirrorCS")])]});
            var sketch = newSketch(context, id + "F12", { "sketchPlane" : qUnion([Q0])});
            skLineSegment(sketch, "E198", {"start": v(-74.41, 0) * mm, "end": v(-58.6, 10) * mm, "construction": true});
            skCircle(sketch, "E199", {"center": v(-66.5, 5) * mm, "radius": 2 * mm});
            skSolve(sketch);
        }
        {
            var Q0;
            Q0=makeQuery(id+"F12.imprint","IMPRINT",FACE,{"disambiguationData":[TD([[makeQuery(id+"F12.imprint","IMPRINT",EDGE,{"derivedFrom":sQuery(id+"F12.wireOp",EDGE,"E199")}),1.0]])]});
            extrude(context, id + "F13", {"entities" : qUnion([Q0]), "operationType" : NewBodyOperationType.REMOVE, "oppositeDirection" : true, "depth" : 25 * mm, "hasSecondDirection" : true, "secondDirectionOppositeDirection" : false, "secondDirectionDepth" : 25 * mm});
        }
        {
            var Q0;
            Q0=makeQuery(id+"F5.opExtrude","SWEPT_FACE",FACE,{"disambiguationData":[OSD([sQuery(id+"F2.wireOp",EDGE,"E142.MirrorCS")])]});
            var sketch = newSketch(context, id + "F14", { "sketchPlane" : qUnion([Q0])});
            skLineSegment(sketch, "E200", {"start": v(-100.84, 50) * mm, "end": v(-77.64, 63.5) * mm, "construction": true});
            skCircle(sketch, "E201", {"center": v(-89.24, 56.75) * mm, "radius": 2.5 * mm});
            skLineSegment(sketch, "E202", {"start": v(-100.84, 63.5) * mm, "end": v(-87.5, 63.5) * mm, "construction": true});
            skCircle(sketch, "E203.MirrorC", {"center": v(-89.24, 70.25) * mm, "radius": 2.5 * mm});
            skPoint(sketch, "E204", {"position": v(-74.41, 63.5) * mm});
            skSolve(sketch);
        }
        {
            var Q0;
            Q0=makeQuery(id+"F14.imprint","IMPRINT",FACE,{"disambiguationData":[TD([[makeQuery(id+"F14.imprint","IMPRINT",EDGE,{"derivedFrom":sQuery(id+"F14.wireOp",EDGE,"E201")}),1.0]])]});
            var Q1;
            Q1=makeQuery(id+"F14.imprint","IMPRINT",FACE,{"disambiguationData":[TD([[makeQuery(id+"F14.imprint","IMPRINT",EDGE,{"derivedFrom":sQuery(id+"F14.wireOp",EDGE,"E203.MirrorC")}),-1.0]])]});
            var Q2;
            Q2=sQuery(id+"F14.wireOp",EDGE,"E201");
            extrude(context, id + "F15", {"entities" : qUnion([Q0, Q1]), "operationType" : NewBodyOperationType.REMOVE, "surfaceEntities" : qUnion([Q2]), "oppositeDirection" : true, "depth" : 25 * mm, "hasSecondDirection" : true, "secondDirectionOppositeDirection" : false, "secondDirectionDepth" : 25 * mm});
        }
        {
            var Q0;
            Q0=makeQuery(id+"F6.imprint","IMPRINT",FACE,{"disambiguationData":[TD([[makeQuery(id+"F6.imprint","IMPRINT",EDGE,{"derivedFrom":sQuery(id+"F6.wireOp",EDGE,"E188.MirrorC")}),-1.0]])]});
            var Q1;
            Q1=makeQuery(id+"F6.imprint","IMPRINT",FACE,{"disambiguationData":[TD([[makeQuery(id+"F6.imprint","IMPRINT",EDGE,{"derivedFrom":sQuery(id+"F6.wireOp",EDGE,"E166")}),-1.0]])]});
            var Q2;
            Q2=makeQuery(id+"F6.imprint","IMPRINT",FACE,{"disambiguationData":[TD([[makeQuery(id+"F6.imprint","IMPRINT",EDGE,{"derivedFrom":sQuery(id+"F6.wireOp",EDGE,"E167")}),-1.0]])]});
            var Q3;
            Q3=makeQuery(id+"F6.imprint","IMPRINT",FACE,{"disambiguationData":[TD([[makeQuery(id+"F6.imprint","IMPRINT",EDGE,{"derivedFrom":sQuery(id+"F6.wireOp",EDGE,"E168")}),-1.0]])]});
            var Q4;
            Q4=makeQuery(id+"F6.imprint","IMPRINT",FACE,{"disambiguationData":[TD([[makeQuery(id+"F6.imprint","IMPRINT",EDGE,{"derivedFrom":sQuery(id+"F6.wireOp",EDGE,"E187.MirrorC")}),-1.0]])]});
            var Q5;
            Q5=makeQuery(id+"F6.imprint","IMPRINT",FACE,{"disambiguationData":[TD([[makeQuery(id+"F6.imprint","IMPRINT",EDGE,{"derivedFrom":sQuery(id+"F6.wireOp",EDGE,"E186.MirrorC")}),-1.0]])]});
            var Q6;
            Q6=makeQuery(id+"F6.imprint","IMPRINT",FACE,{"disambiguationData":[TD([[makeQuery(id+"F6.imprint","IMPRINT",EDGE,{"derivedFrom":sQuery(id+"F6.wireOp",EDGE,"E175")}),-1.0]])]});
            var Q7;
            Q7=makeQuery(id+"F6.imprint","IMPRINT",FACE,{"disambiguationData":[TD([[makeQuery(id+"F6.imprint","IMPRINT",EDGE,{"derivedFrom":sQuery(id+"F6.wireOp",EDGE,"E177.MirrorC")}),1.0]])]});
            var Q8;
            Q8=makeQuery(id+"F6.imprint","IMPRINT",FACE,{"disambiguationData":[TD([[makeQuery(id+"F6.imprint","IMPRINT",EDGE,{"derivedFrom":sQuery(id+"F6.wireOp",EDGE,"E178.MirrorC")}),1.0]])]});
            var Q9;
            Q9=makeQuery(id+"F6.imprint","IMPRINT",FACE,{"disambiguationData":[TD([[makeQuery(id+"F6.imprint","IMPRINT",EDGE,{"derivedFrom":sQuery(id+"F6.wireOp",EDGE,"E176")}),-1.0]])]});
            extrude(context, id + "F16", {"entities" : qUnion([Q0, Q1, Q2, Q3, Q4, Q5, Q6, Q7, Q8, Q9]), "operationType" : NewBodyOperationType.REMOVE, "oppositeDirection" : true, "depth" : 14.88 * mm, "hasSecondDirection" : true, "secondDirectionOppositeDirection" : true, "secondDirectionDepth" : 5 * mm});
        }
        {
            var Q0;
            Q0=makeQuery(id+"F0.imprint","IMPRINT",FACE,{"disambiguationData":[TD([[makeQuery(id+"F0.imprint","IMPRINT",EDGE,{"derivedFrom":sQuery(id+"F0.wireOp",EDGE,"E115")}),1.0]])]});
            extrude(context, id + "F17", {"entities" : qUnion([Q0]), "depth" : 70 * mm});
        }
        {
            var Q0;
            Q0=makeQuery(id+"F0.imprint","IMPRINT",FACE,{"disambiguationData":[TD([[makeQuery(id+"F0.imprint","IMPRINT",EDGE,{"derivedFrom":sQuery(id+"F0.wireOp",EDGE,"E116")}),1.0]])]});
            extrude(context, id + "F18", {"entities" : qUnion([Q0]), "operationType" : NewBodyOperationType.ADD, "depth" : 135 * mm});
        }
        {
            var Q0;
            Q0=makeQuery(id+"F1.opExtrude","CAP_FACE",FACE,{"disambiguationData":[OSD([sQuery(id+"F0.wireOp",EDGE,"E91"),sQuery(id+"F0.wireOp",EDGE,"E92"),sQuery(id+"F0.wireOp",EDGE,"E93"),sQuery(id+"F0.wireOp",EDGE,"E94"),sQuery(id+"F0.wireOp",EDGE,"E97"),sQuery(id+"F0.wireOp",EDGE,"E98.MirrorC"),sQuery(id+"F0.wireOp",EDGE,"E99"),sQuery(id+"F0.wireOp",EDGE,"E100.MirrorC"),sQuery(id+"F0.wireOp",EDGE,"E101"),sQuery(id+"F0.wireOp",EDGE,"E102"),sQuery(id+"F0.wireOp",EDGE,"E103.MirrorC"),sQuery(id+"F0.wireOp",EDGE,"E104.bottom"),sQuery(id+"F0.wireOp",EDGE,"E105"),sQuery(id+"F0.wireOp",EDGE,"E106"),sQuery(id+"F0.wireOp",EDGE,"E107"),sQuery(id+"F0.wireOp",EDGE,"E108"),sQuery(id+"F0.wireOp",EDGE,"E109"),sQuery(id+"F0.wireOp",EDGE,"E110"),sQuery(id+"F0.wireOp",EDGE,"E111"),sQuery(id+"F0.wireOp",EDGE,"E113.filletArc"),sQuery(id+"F0.wireOp",EDGE,"E114.MirrorC"),sQuery(id+"F0.wireOp",EDGE,"E121.bottom"),sQuery(id+"F0.wireOp",EDGE,"E121.top"),sQuery(id+"F0.wireOp",EDGE,"E121.right"),sQuery(id+"F0.wireOp",EDGE,"E123.MirrorCS"),sQuery(id+"F0.wireOp",EDGE,"E124.MirrorCS"),sQuery(id+"F0.wireOp",EDGE,"E125.MirrorCS")])],"isStart":false});
            extrude(context, id + "F19", {"entities" : qUnion([Q0]), "operationType" : NewBodyOperationType.ADD, "depth" : 4 * mm});
        }
    });
